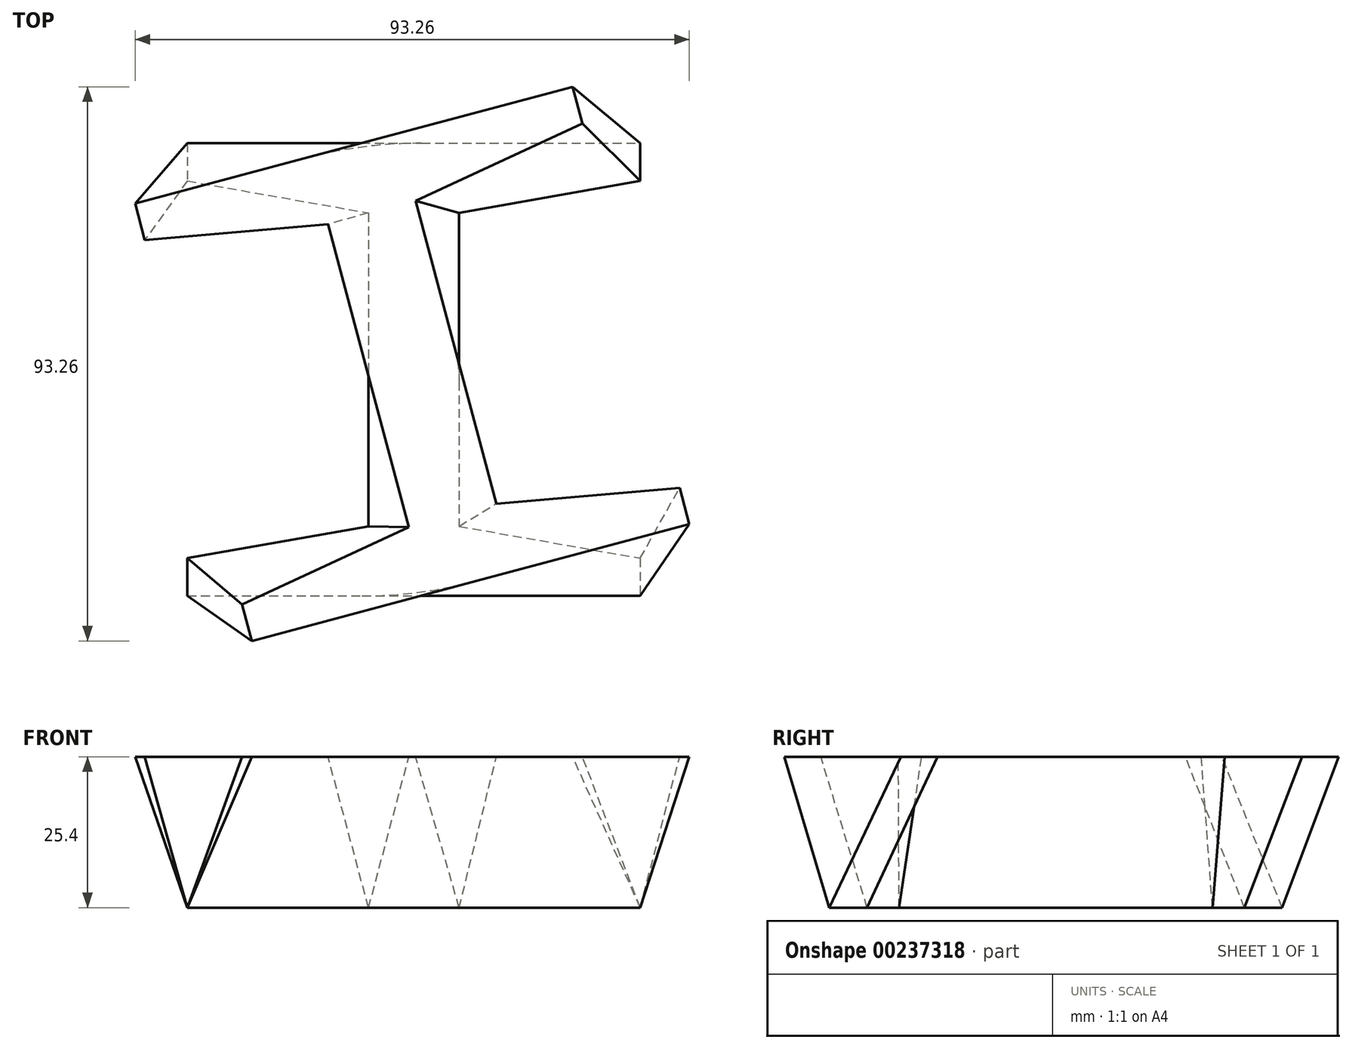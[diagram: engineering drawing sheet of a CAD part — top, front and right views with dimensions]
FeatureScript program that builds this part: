
annotation { "Feature Type Name" : "Feature", "Feature Type Description" : "" }
export const myFeature = defineFeature(function(context is Context, id is Id, definition is map)
    precondition{}
    {
        {
            var Q0;
            Q0=qCreatedBy(makeId("Top.planeOp"),FACE);
            var sketch = newSketch(context, id + "F0", { "sketchPlane" : qUnion([Q0])});
            skLineSegment(sketch, "E0", {"start": v(38.1, 0) * mm, "end": v(0, 0) * mm});
            skLineSegment(sketch, "E1", {"start": v(0, 0) * mm, "end": v(0, -6.35) * mm});
            skLineSegment(sketch, "E2", {"start": v(0, -6.35) * mm, "end": v(30.48, -11.72) * mm});
            skLineSegment(sketch, "E3", {"start": v(30.48, -11.72) * mm, "end": v(30.48, -64.48) * mm});
            skLineSegment(sketch, "E4", {"start": v(30.48, -64.48) * mm, "end": v(0, -69.85) * mm});
            skLineSegment(sketch, "E5", {"start": v(0, -69.85) * mm, "end": v(0, -76.2) * mm});
            skLineSegment(sketch, "E6", {"start": v(0, -76.2) * mm, "end": v(38.1, -76.2) * mm});
            skLineSegment(sketch, "E7", {"start": v(38.1, 0) * mm, "end": v(38.1, -76.2) * mm, "construction": true});
            skLineSegment(sketch, "E8.MirrorCS", {"start": v(38.1, 0) * mm, "end": v(76.2, 0) * mm});
            skLineSegment(sketch, "E9.MirrorCS", {"start": v(76.2, 0) * mm, "end": v(76.2, -6.35) * mm});
            skLineSegment(sketch, "E10.MirrorCS", {"start": v(76.2, -6.35) * mm, "end": v(45.72, -11.72) * mm});
            skLineSegment(sketch, "E11.MirrorCS", {"start": v(45.72, -11.72) * mm, "end": v(45.72, -64.48) * mm});
            skLineSegment(sketch, "E12.MirrorCS", {"start": v(45.72, -64.48) * mm, "end": v(76.2, -69.85) * mm});
            skLineSegment(sketch, "E13.MirrorCS", {"start": v(76.2, -69.85) * mm, "end": v(76.2, -76.2) * mm});
            skLineSegment(sketch, "E14.MirrorCS", {"start": v(76.2, -76.2) * mm, "end": v(38.1, -76.2) * mm});
            skSolve(sketch);
        }
        {
            var Q0;
            Q0=qCreatedBy(makeId("Top.planeOp"),FACE);
            cPlane(context, id + "F1", {"entities" : qUnion([Q0]), "cplaneType" : CPlaneType.OFFSET, "offset" : 25.4 * mm, "width" : 152.4 * mm, "height" : 152.4 * mm});
        }
        {
            var Q0;
            Q0=qCreatedBy(id+"F1.planeOp",FACE);
            var sketch = newSketch(context, id + "F2", { "sketchPlane" : qUnion([Q0])});
            skLineSegment(sketch, "E15", {"start": v(-8.8, -10.15) * mm, "end": v(-7.16, -16.28) * mm});
            skLineSegment(sketch, "E16", {"start": v(-7.16, -16.28) * mm, "end": v(23.67, -13.62) * mm});
            skLineSegment(sketch, "E17", {"start": v(23.67, -13.62) * mm, "end": v(37.27, -64.6) * mm});
            skLineSegment(sketch, "E18", {"start": v(37.27, -64.6) * mm, "end": v(9.2, -77.64) * mm});
            skLineSegment(sketch, "E19", {"start": v(9.2, -77.64) * mm, "end": v(10.84, -83.77) * mm});
            skLineSegment(sketch, "E20", {"start": v(10.84, -83.77) * mm, "end": v(47.65, -73.96) * mm});
            skLineSegment(sketch, "E21", {"start": v(-8.8, -10.15) * mm, "end": v(28.02, -0.33) * mm});
            skLineSegment(sketch, "E22", {"start": v(28.02, -0.33) * mm, "end": v(47.65, -73.96) * mm, "construction": true});
            skLineSegment(sketch, "E23.MirrorCS", {"start": v(64.83, 9.49) * mm, "end": v(28.02, -0.33) * mm});
            skLineSegment(sketch, "E24.MirrorCS", {"start": v(64.83, 9.49) * mm, "end": v(66.46, 3.35) * mm});
            skLineSegment(sketch, "E25.MirrorCS", {"start": v(66.46, 3.35) * mm, "end": v(38.4, -9.7) * mm});
            skLineSegment(sketch, "E26.MirrorCS", {"start": v(38.4, -9.7) * mm, "end": v(52, -60.66) * mm});
            skLineSegment(sketch, "E27.MirrorCS", {"start": v(52, -60.66) * mm, "end": v(82.83, -58) * mm});
            skLineSegment(sketch, "E28.MirrorCS", {"start": v(82.83, -58) * mm, "end": v(84.46, -64.14) * mm});
            skLineSegment(sketch, "E29.MirrorCS", {"start": v(84.46, -64.14) * mm, "end": v(47.65, -73.96) * mm});
            skSolve(sketch);
        }
        {
            var Q0;
            Q0=makeQuery(id+"F0.imprint","IMPRINT",FACE,{"disambiguationData":[TD([[makeQuery(id+"F0.imprint","IMPRINT",EDGE,{"derivedFrom":sQuery(id+"F0.wireOp",EDGE,"E0")}),1.0]])]});
            var Q1;
            Q1=makeQuery(id+"F2.imprint","IMPRINT",FACE,{"disambiguationData":[TD([[makeQuery(id+"F2.imprint","IMPRINT",EDGE,{"derivedFrom":sQuery(id+"F2.wireOp",EDGE,"E15")}),1.0]])]});
            loft(context, id + "F3", {"sheetProfilesArray" : [{ "sheetProfileEntities" : qUnion([Q0]) }, { "sheetProfileEntities" : qUnion([Q1]) }]});
        }
    });
